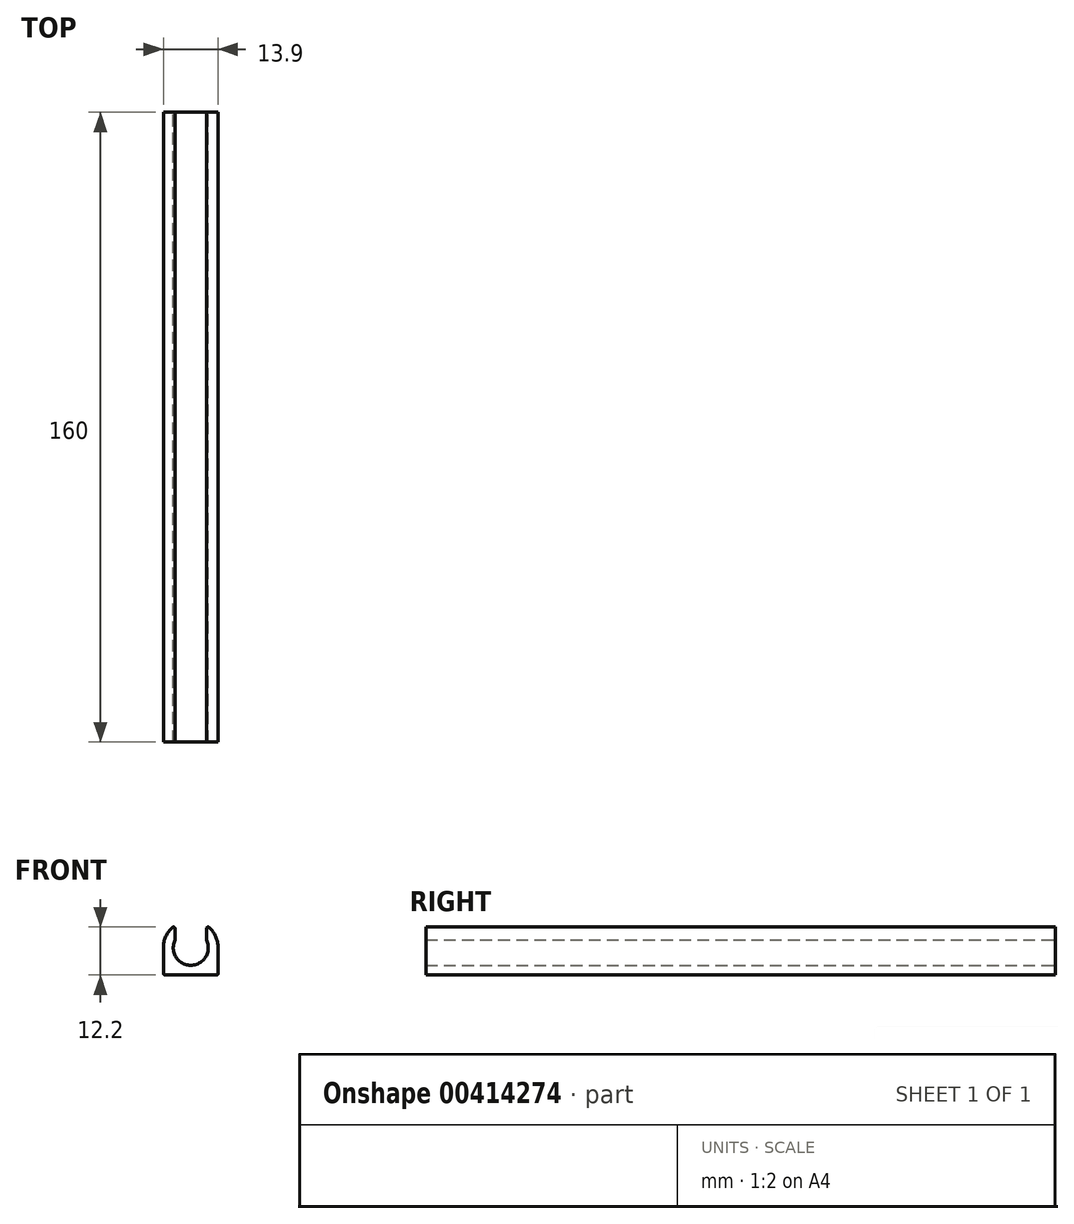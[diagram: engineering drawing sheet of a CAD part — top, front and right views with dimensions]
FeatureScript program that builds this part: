
annotation { "Feature Type Name" : "Feature", "Feature Type Description" : "" }
export const myFeature = defineFeature(function(context is Context, id is Id, definition is map)
    precondition{}
    {
        {
            var Q0;
            Q0=qCreatedBy(makeId("Front.planeOp"),FACE);
            var sketch = newSketch(context, id + "F0", { "sketchPlane" : qUnion([Q0])});
            skArc(sketch, "E0", {"start": v(-4, 1.95) * mm, "mid": v(0, -4.45) * mm, "end": v(4, 1.95) * mm});
            skArc(sketch, "E1.0", {"start": v(-4.67, 5.15) * mm, "mid": v(-6.35, 2.82) * mm, "end": v(-6.95, 0) * mm});
            skLineSegment(sketch, "E2", {"start": v(0, 0) * mm, "end": v(0, 6.95) * mm, "construction": true});
            skLineSegment(sketch, "E3.0", {"start": v(4, 1.95) * mm, "end": v(4, 4.85) * mm});
            skLineSegment(sketch, "E4.MirrorCS", {"start": v(-4, 1.95) * mm, "end": v(-4, 4.85) * mm});
            skPoint(sketch, "E5.orphan", {"position": v(-4, 6.4) * mm});
            skPoint(sketch, "E6.orphan", {"position": v(-4, 0) * mm});
            skPoint(sketch, "E7.orphan", {"position": v(4, 0) * mm});
            skPoint(sketch, "E8.orphan", {"position": v(4, 6.4) * mm});
            skPoint(sketch, "E9.visualSharp", {"position": v(-4, 5.68) * mm});
            skArc(sketch, "E9.filletArc", {"start": v(-4, 4.85) * mm, "mid": v(-4.24, 5.22) * mm, "end": v(-4.67, 5.15) * mm});
            skPoint(sketch, "E10.visualSharp", {"position": v(4, 5.68) * mm});
            skArc(sketch, "E10.filletArc", {"start": v(4.67, 5.15) * mm, "mid": v(4.24, 5.22) * mm, "end": v(4, 4.85) * mm});
            skLineSegment(sketch, "E11", {"start": v(-6.95, 0) * mm, "end": v(-6.95, -6.55) * mm});
            skPoint(sketch, "E11.endSnap0", {"position": v(0, -6.95) * mm});
            skLineSegment(sketch, "E12", {"start": v(6.95, 0) * mm, "end": v(6.95, -6.55) * mm});
            skLineSegment(sketch, "E13", {"start": v(6.55, -6.95) * mm, "end": v(-6.55, -6.95) * mm});
            skArc(sketch, "E14.trimOffspring", {"start": v(6.95, 0) * mm, "mid": v(6.35, 2.82) * mm, "end": v(4.67, 5.15) * mm});
            skPoint(sketch, "E15.visualSharp", {"position": v(-6.95, -6.95) * mm});
            skArc(sketch, "E15.filletArc", {"start": v(-6.95, -6.55) * mm, "mid": v(-6.83, -6.83) * mm, "end": v(-6.55, -6.95) * mm});
            skPoint(sketch, "E16.visualSharp", {"position": v(6.95, -6.95) * mm});
            skArc(sketch, "E16.filletArc", {"start": v(6.55, -6.95) * mm, "mid": v(6.83, -6.83) * mm, "end": v(6.95, -6.55) * mm});
            skSolve(sketch);
        }
        {
            var Q0;
            Q0=makeQuery(id+"F0.imprint","IMPRINT",FACE,{"disambiguationData":[TD([[makeQuery(id+"F0.imprint","IMPRINT",EDGE,{"derivedFrom":sQuery(id+"F0.wireOp",EDGE,"E0")}),-1.0]])]});
            extrude(context, id + "F1", {"entities" : qUnion([Q0]), "flatOperationType" : FlatOperationType.REMOVE, "offsetDistance" : 25 * mm, "depth" : 160 * mm, "domain" : OperationDomain.MODEL});
        }
    });
